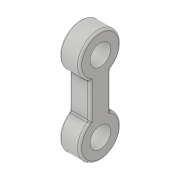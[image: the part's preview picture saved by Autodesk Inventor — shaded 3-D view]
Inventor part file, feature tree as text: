
AUTODESK INVENTOR PART (.ipt)
format: ipt  version: 2017 (Build 210142000, 142)  size: 171,520 bytes
history: native  units: in
note: dims shown in document units (in); Inventor stores cm internally (conversion verified against a paired STEP export)
features: fillet x2, extrude x1, sketch x1
ambient origin geometry x8: Origin, YZ Plane, XZ Plane, XY Plane, X Axis, Y Axis, Z Axis, Center Point
bodies: Solid1 (feature_tree)
feature tree (4):
  extrude  "Extrusion1"  Depth=0.4in
  fillet  "Fillet1"  Radius=1.38in
  fillet  "Fillet2"  Radius=0.4in
  sketch  "Sketch1"  dims[d0=0.4in d1=0.4in d2=1.38in d3=0.4in d4=0.2in d5=0.4in d6=0.0in d7=0.04in d8=0.04in]
